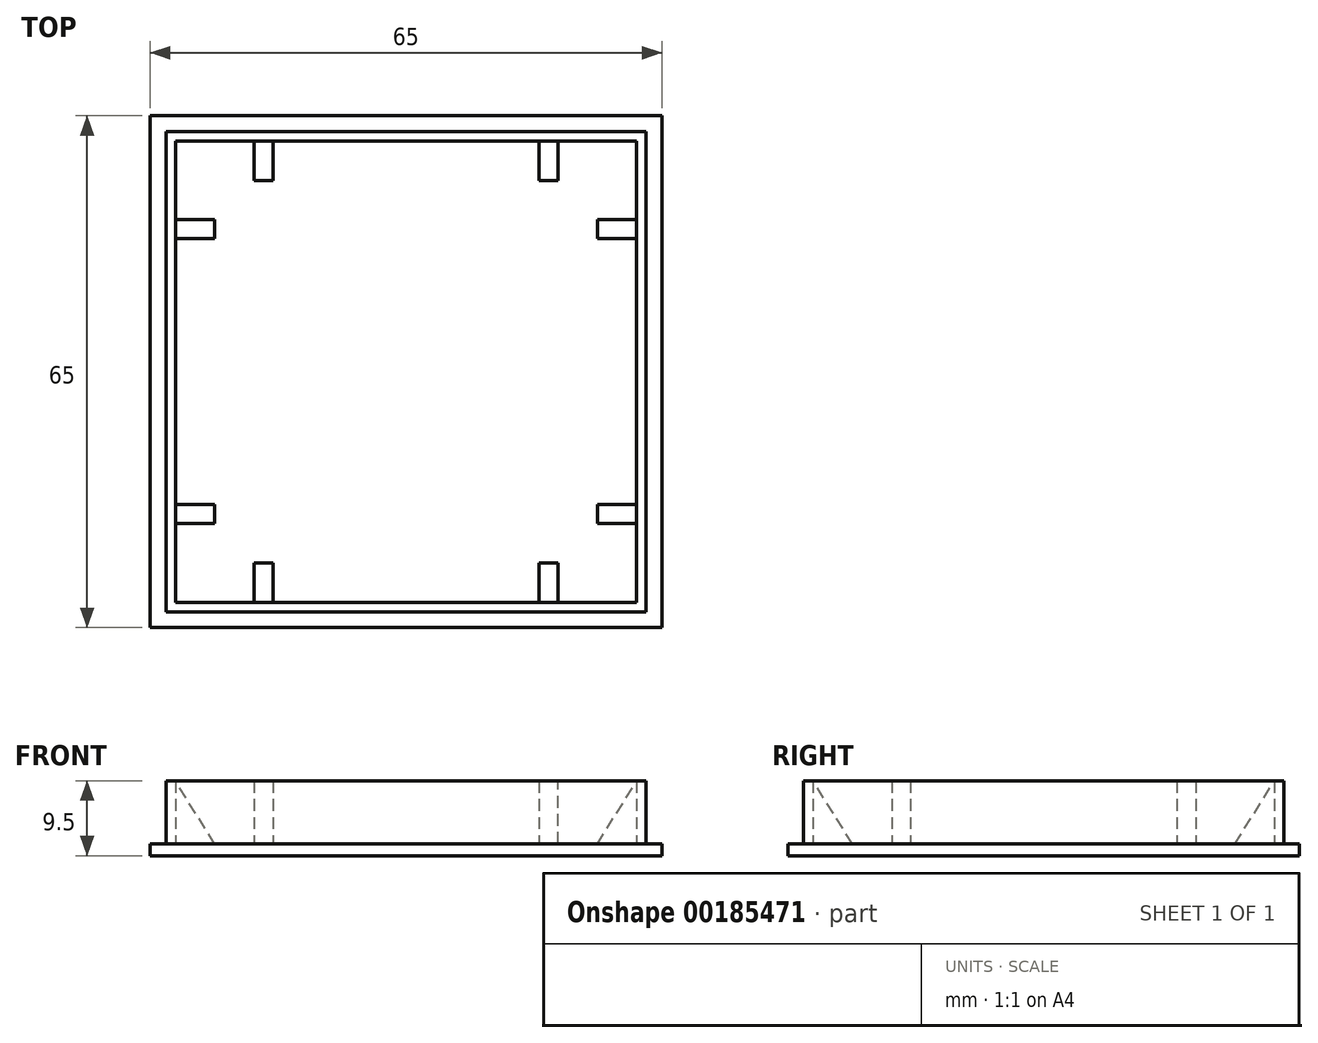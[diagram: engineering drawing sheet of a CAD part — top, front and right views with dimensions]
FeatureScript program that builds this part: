
annotation { "Feature Type Name" : "Feature", "Feature Type Description" : "" }
export const myFeature = defineFeature(function(context is Context, id is Id, definition is map)
    precondition{}
    {
        {
            var Q0;
            Q0=qCreatedBy(makeId("Top.planeOp"),FACE);
            var sketch = newSketch(context, id + "F0", { "sketchPlane" : qUnion([Q0])});
            skLineSegment(sketch, "E0.bottom", {"start": v(32.5, 32.5) * mm, "end": v(-32.5, 32.5) * mm});
            skLineSegment(sketch, "E0.top", {"start": v(32.5, -32.5) * mm, "end": v(-32.5, -32.5) * mm});
            skLineSegment(sketch, "E0.left", {"start": v(32.5, 32.5) * mm, "end": v(32.5, -32.5) * mm});
            skLineSegment(sketch, "E0.right", {"start": v(-32.5, 32.5) * mm, "end": v(-32.5, -32.5) * mm});
            skPoint(sketch, "E0.middle", {"position": v(0, 0) * mm});
            skSolve(sketch);
        }
        {
            var Q0;
            Q0 = qSketchRegion(id + "F0", true);
            extrude(context, id + "F1", {"entities" : qUnion([Q0]), "depth" : 1.5 * mm});
        }
        {
            var Q0;
            Q0=makeQuery(id+"F1.opExtrude","CAP_FACE",FACE,{"disambiguationData":[OSD([sQuery(id+"F0.wireOp",EDGE,"E0.bottom"),sQuery(id+"F0.wireOp",EDGE,"E0.top"),sQuery(id+"F0.wireOp",EDGE,"E0.left"),sQuery(id+"F0.wireOp",EDGE,"E0.right")])],"isStart":false});
            var sketch = newSketch(context, id + "F2", { "sketchPlane" : qUnion([Q0])});
            skLineSegment(sketch, "E1.bottom", {"start": v(-30.5, 30.5) * mm, "end": v(30.5, 30.5) * mm});
            skLineSegment(sketch, "E1.top", {"start": v(-30.5, -30.5) * mm, "end": v(30.5, -30.5) * mm});
            skLineSegment(sketch, "E1.left", {"start": v(-30.5, 30.5) * mm, "end": v(-30.5, -30.5) * mm});
            skLineSegment(sketch, "E1.right", {"start": v(30.5, 30.5) * mm, "end": v(30.5, -30.5) * mm});
            skPoint(sketch, "E1.middle", {"position": v(0, 0) * mm});
            skLineSegment(sketch, "E2.0", {"start": v(-29.3, 29.3) * mm, "end": v(-29.3, 19.3) * mm});
            skLineSegment(sketch, "E2.1", {"start": v(-29.3, 29.3) * mm, "end": v(-19.3, 29.3) * mm});
            skLineSegment(sketch, "E2.2", {"start": v(29.3, 29.3) * mm, "end": v(29.3, 19.3) * mm});
            skLineSegment(sketch, "E2.3", {"start": v(-29.3, -29.3) * mm, "end": v(-19.3, -29.3) * mm});
            skLineSegment(sketch, "E3", {"start": v(-29.3, 19.3) * mm, "end": v(-24.3, 19.3) * mm});
            skLineSegment(sketch, "E4", {"start": v(-29.3, 16.9) * mm, "end": v(-24.3, 16.9) * mm});
            skLineSegment(sketch, "E5.trimOffspring", {"start": v(-29.3, 16.9) * mm, "end": v(-29.3, -16.9) * mm});
            skLineSegment(sketch, "E6.trimOffspring", {"start": v(29.3, 16.9) * mm, "end": v(29.3, -16.9) * mm});
            skLineSegment(sketch, "E7", {"start": v(-24.3, 19.3) * mm, "end": v(-24.3, 16.9) * mm});
            skLineSegment(sketch, "E8", {"start": v(24.3, 19.3) * mm, "end": v(24.3, 16.9) * mm});
            skLineSegment(sketch, "E9.trimOffspring", {"start": v(24.3, 19.3) * mm, "end": v(29.3, 19.3) * mm});
            skLineSegment(sketch, "E10.trimOffspring", {"start": v(24.3, 16.9) * mm, "end": v(29.3, 16.9) * mm});
            skLineSegment(sketch, "E11.MirrorCS", {"start": v(24.3, -16.9) * mm, "end": v(29.3, -16.9) * mm});
            skLineSegment(sketch, "E12.MirrorCS", {"start": v(24.3, -19.3) * mm, "end": v(24.3, -16.9) * mm});
            skLineSegment(sketch, "E13.MirrorCS", {"start": v(24.3, -19.3) * mm, "end": v(29.3, -19.3) * mm});
            skLineSegment(sketch, "E14.MirrorCS", {"start": v(-24.3, -19.3) * mm, "end": v(-24.3, -16.9) * mm});
            skLineSegment(sketch, "E15.MirrorCS", {"start": v(-29.3, -19.3) * mm, "end": v(-24.3, -19.3) * mm});
            skLineSegment(sketch, "E16.MirrorCS", {"start": v(-29.3, -16.9) * mm, "end": v(-24.3, -16.9) * mm});
            skLineSegment(sketch, "E17", {"start": v(-19.3, 29.3) * mm, "end": v(-19.3, 24.3) * mm});
            skLineSegment(sketch, "E18", {"start": v(-16.9, -29.3) * mm, "end": v(-16.9, -24.3) * mm});
            skLineSegment(sketch, "E19", {"start": v(-19.3, 24.3) * mm, "end": v(-16.9, 24.3) * mm});
            skLineSegment(sketch, "E20", {"start": v(-19.3, -24.3) * mm, "end": v(-16.9, -24.3) * mm});
            skLineSegment(sketch, "E21.trimOffspring", {"start": v(-19.3, -24.3) * mm, "end": v(-19.3, -29.3) * mm});
            skLineSegment(sketch, "E22.trimOffspring", {"start": v(-16.9, 24.3) * mm, "end": v(-16.9, 29.3) * mm});
            skLineSegment(sketch, "E23.MirrorCS", {"start": v(16.9, 24.3) * mm, "end": v(16.9, 29.3) * mm});
            skLineSegment(sketch, "E24.MirrorCS", {"start": v(19.3, 24.3) * mm, "end": v(16.9, 24.3) * mm});
            skLineSegment(sketch, "E25.MirrorCS", {"start": v(19.3, 29.3) * mm, "end": v(19.3, 24.3) * mm});
            skLineSegment(sketch, "E26.MirrorCS", {"start": v(16.9, -29.3) * mm, "end": v(16.9, -24.3) * mm});
            skLineSegment(sketch, "E27.MirrorCS", {"start": v(19.3, -24.3) * mm, "end": v(19.3, -29.3) * mm});
            skLineSegment(sketch, "E28.MirrorCS", {"start": v(19.3, -24.3) * mm, "end": v(16.9, -24.3) * mm});
            skLineSegment(sketch, "E29.trimOffspring", {"start": v(-29.3, -19.3) * mm, "end": v(-29.3, -29.3) * mm});
            skLineSegment(sketch, "E30.trimOffspring", {"start": v(-16.9, -29.3) * mm, "end": v(16.9, -29.3) * mm});
            skLineSegment(sketch, "E31.trimOffspring", {"start": v(19.3, -29.3) * mm, "end": v(29.3, -29.3) * mm});
            skLineSegment(sketch, "E32.trimOffspring", {"start": v(29.3, -19.3) * mm, "end": v(29.3, -29.3) * mm});
            skLineSegment(sketch, "E33.trimOffspring", {"start": v(19.3, 29.3) * mm, "end": v(29.3, 29.3) * mm});
            skLineSegment(sketch, "E34.trimOffspring", {"start": v(-16.9, 29.3) * mm, "end": v(16.9, 29.3) * mm});
            skSolve(sketch);
        }
        {
            var Q0;
            Q0 = qSketchRegion(id + "F2", true);
            extrude(context, id + "F3", {"entities" : qUnion([Q0]), "operationType" : NewBodyOperationType.ADD, "depth" : 8 * mm});
        }
        {
            var Q0;
            Q0=makeQuery(id+"F3.opExtrude","CAP_EDGE",EDGE,{"disambiguationData":[OSD([sQuery(id+"F2.wireOp",EDGE,"E7")])],"isStart":false});
            var Q1;
            Q1=makeQuery(id+"F3.opExtrude","CAP_EDGE",EDGE,{"disambiguationData":[OSD([sQuery(id+"F2.wireOp",EDGE,"E19")])],"isStart":false});
            var Q2;
            Q2=makeQuery(id+"F3.opExtrude","CAP_EDGE",EDGE,{"disambiguationData":[OSD([sQuery(id+"F2.wireOp",EDGE,"E24.MirrorCS")])],"isStart":false});
            var Q3;
            Q3=makeQuery(id+"F3.opExtrude","CAP_EDGE",EDGE,{"disambiguationData":[OSD([sQuery(id+"F2.wireOp",EDGE,"E8")])],"isStart":false});
            var Q4;
            Q4=makeQuery(id+"F3.opExtrude","CAP_EDGE",EDGE,{"disambiguationData":[OSD([sQuery(id+"F2.wireOp",EDGE,"E20")])],"isStart":false});
            var Q5;
            Q5=makeQuery(id+"F3.opExtrude","CAP_EDGE",EDGE,{"disambiguationData":[OSD([sQuery(id+"F2.wireOp",EDGE,"E14.MirrorCS")])],"isStart":false});
            var Q6;
            Q6=makeQuery(id+"F3.opExtrude","CAP_EDGE",EDGE,{"disambiguationData":[OSD([sQuery(id+"F2.wireOp",EDGE,"E28.MirrorCS")])],"isStart":false});
            var Q7;
            Q7=makeQuery(id+"F3.opExtrude","CAP_EDGE",EDGE,{"disambiguationData":[OSD([sQuery(id+"F2.wireOp",EDGE,"E12.MirrorCS")])],"isStart":false});
            chamfer(context, id + "F4", {"entities" : qUnion([Q0, Q1, Q2, Q3, Q4, Q5, Q6, Q7]), "chamferType" : ChamferType.TWO_OFFSETS, "width1" : 5 * mm, "oppositeDirection" : true, "width2" : 8 * mm, "tangentPropagation" : true});
        }
    });
